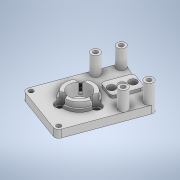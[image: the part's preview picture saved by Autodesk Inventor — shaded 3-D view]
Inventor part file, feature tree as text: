
AUTODESK INVENTOR PART (.ipt)
format: ipt  version: 2022 (Build 260153070, 153G)  size: 360,960 bytes
history: native  units: mm
features: reference x21, extrude x11, sketch x11, other x7, projected_geometry x5
ambient origin geometry x8: Origin, YZ Plane, XZ Plane, XY Plane, X Axis, Y Axis, Z Axis, Center Point
bodies: Solid1 (feature_tree)
feature tree (55):
  extrude  "Extrusion1"  Depth=2.7mm
  extrude  "Extrusion2"  Depth=2.7mm
  extrude  "Extrusion3"  Depth=3.0mm TaperAngle=0.0deg
  extrude  "Extrusion4"  Depth=6.1mm
  extrude  "Extrusion5"  Depth=1.6mm TaperAngle=0.0deg
  extrude  "Extrusion6"  Depth=0.35mm
  extrude  "Extrusion7"  Depth=1.6mm TaperAngle=0.0deg
  extrude  "Extrusion8"  Depth=3.0mm TaperAngle=0.0deg
  extrude  "Extrusion9"  Depth=3.0mm
  extrude  "Extrusion10"  Depth=6.5mm
  extrude  "Extrusion11"  Depth=11.32mm
  sketch  "Sketch1"  dims[d0=3.0mm d1=2.7mm]
  reference  "Reference1"
  reference  "Reference2"
  reference  "Reference3"
  reference  "Reference4"
  reference  "Reference5"
  reference  "Reference6"
  reference  "Reference9"
  reference  "Reference10"
  reference  "Reference11"
  reference  "Reference12"
  reference  "Reference13"
  reference  "Reference14"
  sketch  "Sketch2"  dims[d2=2.7mm d3=30.0mm]
  reference  "Reference15"
  reference  "Reference16"
  reference  "Reference17"
  sketch  "Sketch3"  dims[d4=1.25mm d5=3.0mm d6=0.0mm]
  sketch  "Sketch4"  dims[d7=2.5mm d8=6.1mm]
  sketch  "Sketch5"  dims[d10=1.25mm d11=1.6mm d12=0.0mm]
  reference  "Reference18"
  reference  "Reference19"
  reference  "Reference20"
  sketch  "Sketch6"  dims[d13=1.25mm d14=0.35mm]
  sketch  "Sketch7"  dims[d15=19.0mm d16=1.6mm d17=0.0mm]
  reference  "Reference21"
  reference  "Reference22"
  reference  "Reference23"
  sketch  "Sketch8"  dims[d18=16.85mm d19=3.0mm d20=0.0mm]
  sketch  "Sketch9"  dims[d21=3.0mm d22=0.0mm d23=5.75mm]
  sketch  "Sketch10"  dims[d24=6.5mm d25=0.0mm d26=0.4mm]
  projected_geometry  "Projected Loop1"
  projected_geometry  "Projected Loop2"
  projected_geometry  "Projected Loop3"
  projected_geometry  "Projected Loop4"
  sketch  "Sketch11"  dims[d27=5.5mm d28=5.5mm d29=2.7mm d30=2.0mm d31=1.6mm d32=0.0mm d33=4.6mm d34=4.6mm d35=3.6mm d36=0.0mm d37=2.3mm d38=10.0mm d39=0.0mm d40=11.32mm d41=0.0mm d42=1.3mm d43=0.0mm]
  projected_geometry  "Projected Loop5"
  other  "<userpath> laptop\Desktop\SumoBot\sumobotLIDAR\AssemblyV4\AsemblyV4.iam"
  other  "AsemblyV4.iam"
  other  "AS5600HolderV2:1"
  other  "SRM-12-06A:1"
  other  "MOTOR:1"
  other  "Spur Gears:1"
  other  "Spur Gear1:1"
